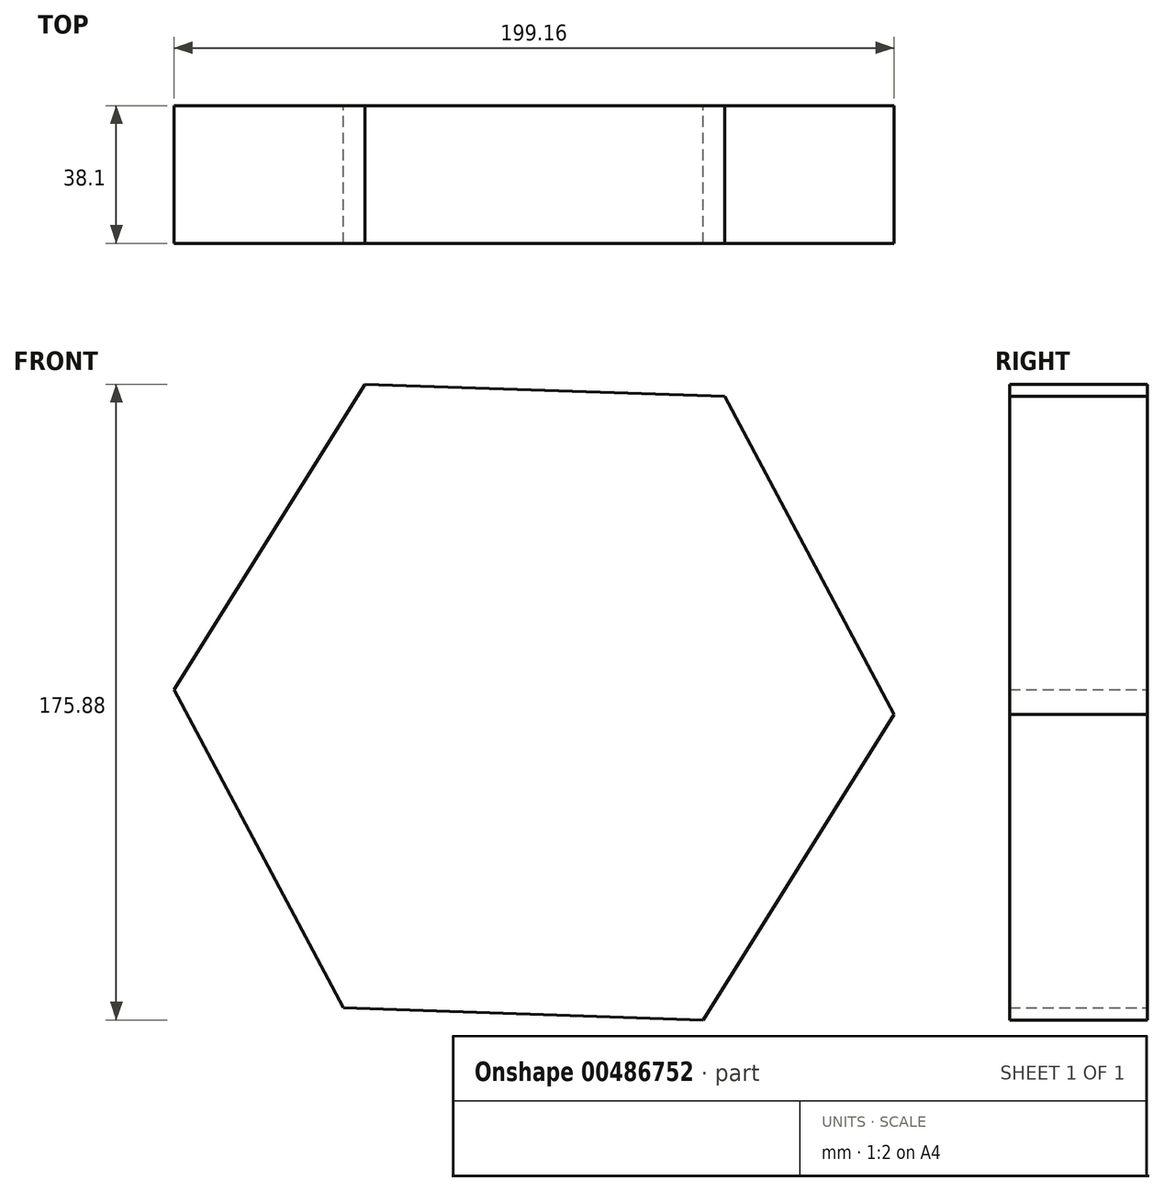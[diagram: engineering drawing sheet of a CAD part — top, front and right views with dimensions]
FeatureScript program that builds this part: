
annotation { "Feature Type Name" : "Feature", "Feature Type Description" : "" }
export const myFeature = defineFeature(function(context is Context, id is Id, definition is map)
    precondition{}
    {
        {
            var Q0;
            Q0=qCreatedBy(makeId("Front.planeOp"),FACE);
            var sketch = newSketch(context, id + "F0", { "sketchPlane" : qUnion([Q0])});
            skCircle(sketch, "E0.cCircle", {"center": v(0, -2.3) * mm, "radius": 86.3 * mm, "construction": true});
            skLineSegment(sketch, "E0.0", {"start": v(52.74, 82.23) * mm, "end": v(99.58, -5.71) * mm});
            skLineSegment(sketch, "E0.1", {"start": v(99.58, -5.71) * mm, "end": v(46.84, -90.25) * mm});
            skLineSegment(sketch, "E0.2", {"start": v(46.84, -90.25) * mm, "end": v(-52.74, -86.85) * mm});
            skLineSegment(sketch, "E0.3", {"start": v(-52.74, -86.85) * mm, "end": v(-99.58, 1.1) * mm});
            skLineSegment(sketch, "E0.4", {"start": v(-99.58, 1.1) * mm, "end": v(-46.84, 85.63) * mm});
            skLineSegment(sketch, "E0.5", {"start": v(-46.84, 85.63) * mm, "end": v(52.74, 82.23) * mm});
            skPoint(sketch, "E0.0.midPoint", {"position": v(76.16, 38.26) * mm});
            skSolve(sketch);
        }
        {
            var Q0;
            Q0 = qSketchRegion(id + "F0", true);
            extrude(context, id + "F1", {"entities" : qUnion([Q0]), "depth" : 38.1 * mm, "offsetDistance" : 25.4 * mm});
        }
    });
